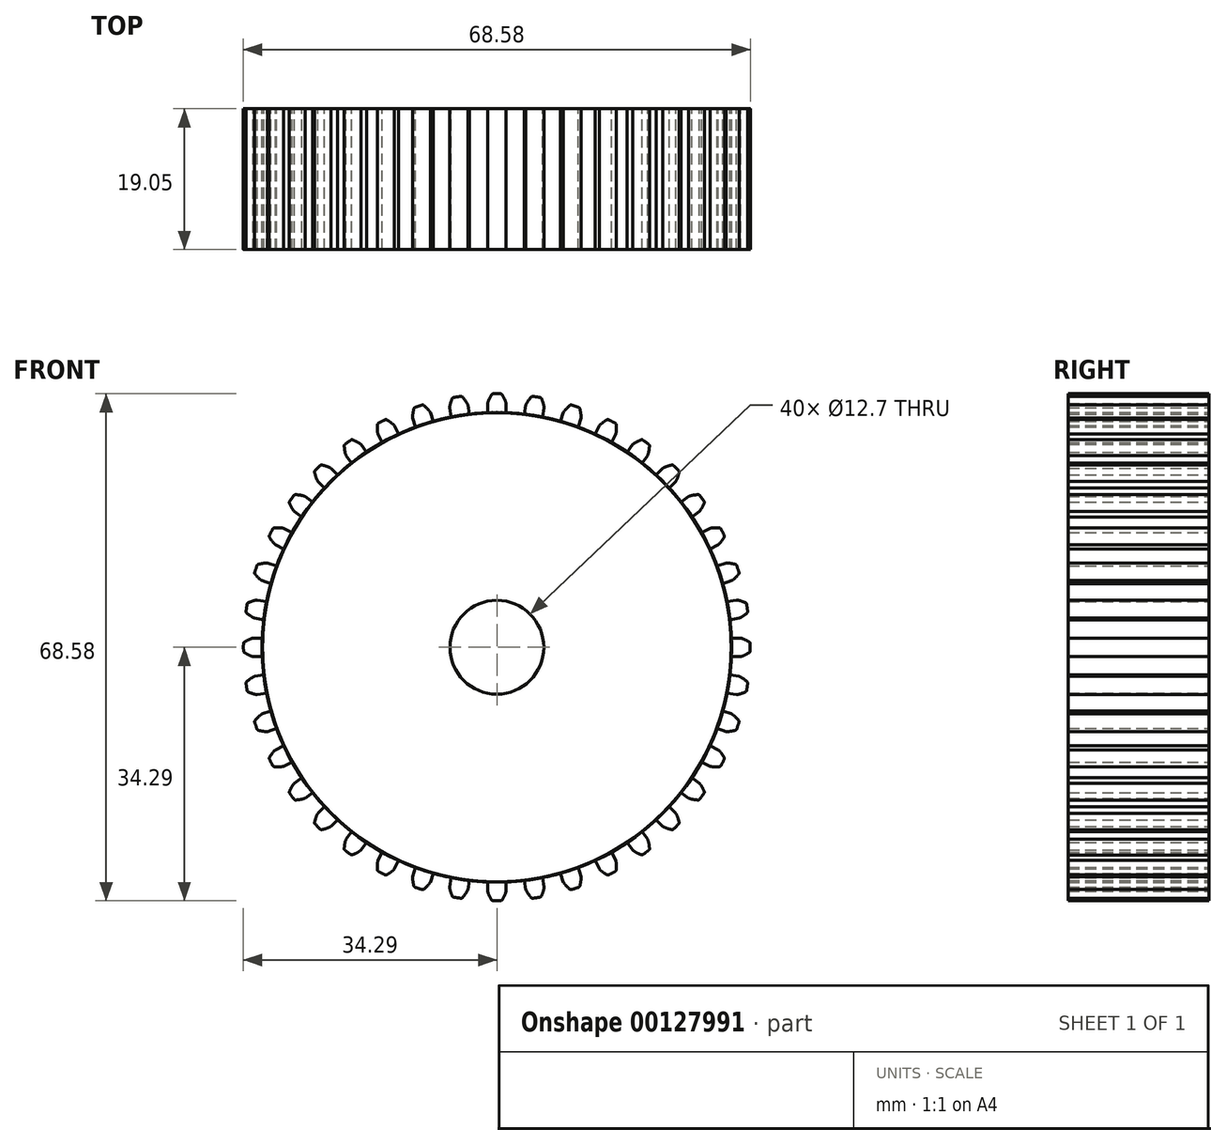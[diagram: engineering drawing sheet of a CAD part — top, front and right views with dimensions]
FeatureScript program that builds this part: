
annotation { "Feature Type Name" : "Feature", "Feature Type Description" : "" }
export const myFeature = defineFeature(function(context is Context, id is Id, definition is map)
    precondition{}
    {
        {
            var Q0;
            Q0=qCreatedBy(makeId("Front.planeOp"),FACE);
            var sketch = newSketch(context, id + "F0", { "sketchPlane" : qUnion([Q0])});
            skCircle(sketch, "E0", {"center": v(0, 0) * mm, "radius": 31.75 * mm});
            skCircle(sketch, "E1", {"center": v(0, 0) * mm, "radius": 34.3 * mm, "construction": true});
            skArc(sketch, "E2", {"start": v(0, 31.75) * mm, "mid": v(-0.62, 31.74) * mm, "end": v(-1.25, 31.73) * mm, "construction": true});
            skLineSegment(sketch, "E3", {"start": v(-1.25, 31.73) * mm, "end": v(-1.25, 33) * mm});
            skArc(sketch, "E4", {"start": v(0, 34.3) * mm, "mid": v(-0.25, 34.29) * mm, "end": v(-0.5, 34.29) * mm});
            skFitSpline(sketch, "E5", {"points": [v(-0.63, 34.28) * mm, v(-1.25, 33) * mm, v(-1.25, 31.73) * mm], "startDerivative": vector(-1.5, -2.48) * mm, "endDerivative": vector(0.29, -2.64) * mm});
            skArc(sketch, "E6.filletArc", {"start": v(-0.5, 34.29) * mm, "mid": v(-0.62, 34.25) * mm, "end": v(-0.7, 34.16) * mm});
            skLineSegment(sketch, "E7.MirrorCS", {"start": v(1.25, 31.73) * mm, "end": v(1.25, 33) * mm});
            skFitSpline(sketch, "E8.MirrorCS", {"points": [v(0.63, 34.28) * mm, v(1.25, 33) * mm, v(1.25, 31.73) * mm], "startDerivative": vector(1.5, -2.48) * mm, "endDerivative": vector(-0.29, -2.64) * mm});
            skArc(sketch, "E9.MirrorCS", {"start": v(0.5, 34.29) * mm, "mid": v(0.62, 34.25) * mm, "end": v(0.7, 34.16) * mm});
            skArc(sketch, "E10.MirrorCS", {"start": v(0, 34.3) * mm, "mid": v(0.25, 34.29) * mm, "end": v(0.5, 34.29) * mm});
            skCircle(sketch, "E11", {"center": v(0, 0) * mm, "radius": 33.02 * mm, "construction": true});
            skCircle(sketch, "E12", {"center": v(0, 0) * mm, "radius": 6.35 * mm});
            skSolve(sketch);
        }
        {
            var Q0;
            {var subQ0=sQuery(id+"F0.wireOp",EDGE,"E0");var subQ1=makeQuery(id+"F0.imprint","INTERSECT",VERTEX,{"derivedFrom":[subQ0,sQuery(id+"F0.wireOp",EDGE,"E3")]});Q0=makeQuery(id+"F0.imprint","IMPRINT",FACE,{"disambiguationData":[TD([[makeQuery(id+"F0.imprint","IMPRINT",EDGE,{"disambiguationData":[TD([[subQ1,1.0]])],"derivedFrom":subQ0}),1.0]])]});}
            var Q1;
            {var subQ0=sQuery(id+"F0.wireOp",EDGE,"E3");Q1=makeQuery(id+"F0.imprint","IMPRINT",FACE,{"disambiguationData":[TD([[makeQuery(id+"F0.imprint","IMPRINT",EDGE,{"derivedFrom":subQ0}),-1.0]])]});}
            extrude(context, id + "F1", {"entities" : qUnion([Q0, Q1]), "depth" : 19.05 * mm});
        }
        {
            var Q0;
            Q0=makeQuery(id+"F1.opExtrude","SWEPT_BODY",BODY,{"disambiguationData":[OSD([sQuery(id+"F0.wireOp",EDGE,"E0"),sQuery(id+"F0.wireOp",EDGE,"E3"),sQuery(id+"F0.wireOp",EDGE,"E4"),sQuery(id+"F0.wireOp",EDGE,"E5"),sQuery(id+"F0.wireOp",EDGE,"E6.filletArc"),sQuery(id+"F0.wireOp",EDGE,"E7.MirrorCS"),sQuery(id+"F0.wireOp",EDGE,"E8.MirrorCS"),sQuery(id+"F0.wireOp",EDGE,"E9.MirrorCS"),sQuery(id+"F0.wireOp",EDGE,"E10.MirrorCS")])]});
            var Q1;
            Q1=makeQuery(id+"F1.opExtrude","SWEPT_FACE",FACE,{"disambiguationData":[OSD([sQuery(id+"F0.wireOp",EDGE,"E0")])]});
            circularPattern(context, id + "F2", {"entities" : qUnion([Q0]), "axis" : qUnion([Q1]), "angle" : 9 * degree, "instanceCount" : 40});
        }
    });
